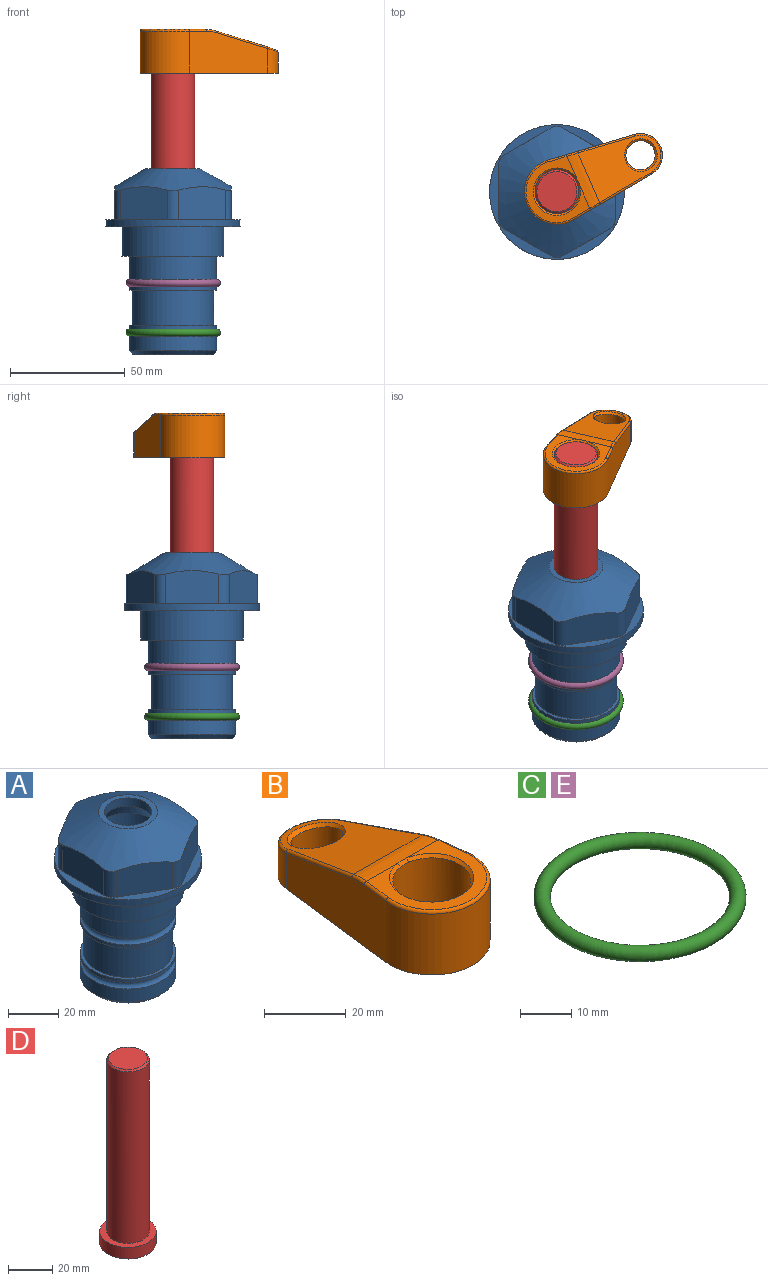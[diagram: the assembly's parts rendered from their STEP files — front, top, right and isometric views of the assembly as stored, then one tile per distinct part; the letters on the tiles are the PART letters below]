
ASSEMBLY  parts=5 mates=4
PART A: 36 faces, bbox 58.7x58.7x81 mm
  f0: cylinder r=17.78mm len=35.56mm, axis (0,0,1), area 1670.8mm2, adj f23,f24,f31
  f1: cylinder r=19.05mm len=38.1mm, axis (0,0,1), area 1191.9mm2, adj f26,f27,f30
  f2: plane 58.66x58.66mm, normal (0,0,-1), area 1150.6mm2, adj f3,f28
  f3: cylinder r=29.33mm len=58.66mm, axis (0,0,-1), area 585.1mm2, adj f2,f4
  f4: plane 58.66x58.66mm, normal (0,0,1), area 475.9mm2, adj f3,f5,f6,f7,f8,f9,f10,f11
  f5: plane 20.32x14.34mm, normal (-0.5,0.87,0), area 324.4mm2, adj f4,f15,f16,f17
  f6: plane 20.32x14.34mm, normal (0.5,0.87,0), area 324.4mm2, adj f4,f14,f15,f17
  f7: plane 23.48x14.34mm, normal (1,0,0), area 324.4mm2, adj f4,f13,f14,f17
  f8: plane 20.32x14.34mm, normal (0.5,-0.87,0), area 324.4mm2, adj f4,f12,f13,f17
  f9: plane 20.32x14.34mm, normal (-0.5,-0.87,0), area 324.4mm2, adj f4,f11,f12,f17
  f10: plane 23.48x14.34mm, normal (-1,0,0), area 324.4mm2, adj f4,f11,f16,f17
  f11: cylinder r=5.08mm len=12.85mm, axis (0,0,-1), area 67.2mm2, adj f4,f9,f10,f17
  f12: cylinder r=5.08mm len=12.85mm, axis (0,0,-1), area 67.2mm2, adj f4,f8,f9,f17
  f13: cylinder r=5.08mm len=12.85mm, axis (0,0,-1), area 67.2mm2, adj f4,f7,f8,f17
  f14: cylinder r=5.08mm len=12.85mm, axis (0,0,-1), area 67.2mm2, adj f4,f6,f7,f17
  f15: cylinder r=5.08mm len=12.85mm, axis (0,0,-1), area 67.2mm2, adj f4,f5,f6,f17
  f16: cylinder r=5.08mm len=12.85mm, axis (0,0,-1), area 67.2mm2, adj f4,f5,f10,f17
  f17: cone r=11.73mm half-angle=60deg, axis (0,0,-1), area 2071.8mm2, adj f5,f6,f7,f8,f9,f10,f11,f12
  f18: plane 23.46x23.46mm, normal (0,0,1), area 147.4mm2, adj f17,f35
  f19: plane 34.93x34.93mm, normal (0,0,-1), area 958mm2, adj f29
  f20: cylinder r=19.05mm len=38.1mm, axis (0,0,1), area 760.1mm2, adj f21,f29
  f21: torus R=19.05mm, axis (0,0,1), area 565.3mm2, adj f20,f22
  f22: cylinder r=19.05mm len=38.1mm, axis (0,0,1), area 190mm2, adj f21,f23
  f23: plane 38.1x38.1mm, normal (0,0,1), area 146.9mm2, adj f0,f22
  f24: plane 38.1x38.1mm, normal (0,0,-1), area 146.9mm2, adj f0,f25
  f25: cylinder r=19.05mm len=38.1mm, axis (0,0,1), area 190mm2, adj f24,f26
  f26: torus R=19.05mm, axis (0,0,1), area 565.3mm2, adj f1,f25
  f27: plane 44.45x44.45mm, normal (0,0,-1), area 411.7mm2, adj f1,f28
  f28: cylinder r=22.23mm len=44.45mm, axis (0,0,1), area 1773.5mm2, adj f2,f27
  f29: cone r=19.05mm half-angle=45deg, axis (0,0,1), area 257.5mm2, adj f19,f20
  f30: cylinder r=3.17mm len=6.75mm, axis (-1,0,0), area 128mm2, adj f1,f33
  f31: cylinder r=3.17mm len=6.35mm, axis (-1,0,0), area 102.5mm2, adj f0,f33
  f32: plane 25.4x25.4mm, normal (0,0,1), area 506.7mm2, adj f33
  f33: cylinder r=12.7mm len=66.42mm, axis (0,0,-1), area 5236.2mm2, adj f30,f31,f32,f34
  f34: cone r=9.53mm half-angle=30deg, axis (0,0,-1), area 443.4mm2, adj f33,f35
  f35: cylinder r=9.53mm len=19.05mm, axis (0,0,-1), area 240.9mm2, adj f18,f34
PART B: 31 faces, bbox 31.7x65.5x19.8 mm
  f0: plane 39.12x18.26mm, normal (0.99,0.12,0), area 612.2mm2, adj f1,f4,f7,f11,f13,f15
  f1: cylinder r=9.53mm len=18.91mm, axis (0,0,-1), area 296.1mm2, adj f0,f2,f7,f17
  f2: plane 39.12x18.26mm, normal (-0.99,0.12,0), area 612.2mm2, adj f1,f4,f7,f12,f14,f16
  f3: cylinder r=6.35mm len=12.7mm, axis (0,0,-1), area 362.4mm2, adj f7,f18
  f4: cylinder r=14.29mm len=28.58mm, axis (0,0,-1), area 882.2mm2, adj f0,f2,f7,f10
  f5: cylinder r=9.53mm len=19.05mm, axis (0,0,-1), area 1092.6mm2, adj f7,f19,f20
  f6: plane 26.99x23.69mm, normal (0,0,1), area 216.2mm2, adj f9,f10,f11,f12,f19
  f7: plane 63.5x28.58mm, normal (0,0,-1), area 661.8mm2, adj f0,f1,f2,f3,f4,f5,f22,f23
  f8: plane 33.52x23.6mm, normal (0,0.26,0.97), area 486mm2, adj f9,f15,f16,f17,f18
  f9: cylinder r=19.05mm len=24.72mm, axis (1,0,0), area 120.4mm2, adj f6,f8,f13,f14,f20
  f10: torus R=13.49mm, axis (0,0,1), area 59mm2, adj f4,f6,f11,f12
  f11: cylinder r=0.79mm len=8.67mm, axis (0.12,-0.99,0), area 10.8mm2, adj f0,f6,f10,f13
  f12: cylinder r=0.79mm len=8.67mm, axis (0.12,0.99,0), area 10.8mm2, adj f2,f6,f10,f14
  f13: bspline ~4.95x1.42mm, area 6.1mm2, adj f0,f9,f11,f15
  f14: bspline ~4.95x1.42mm, area 6.1mm2, adj f2,f9,f12,f16
  f15: cylinder r=0.79mm len=25.95mm, axis (0.12,-0.96,0.26), area 32.9mm2, adj f0,f8,f13,f17
  f16: cylinder r=0.79mm len=25.95mm, axis (0.12,0.96,-0.26), area 32.9mm2, adj f2,f8,f14,f17
  f17: bspline ~18.91x8.38mm, area 30mm2, adj f1,f8,f15,f16
  f18: bspline ~14.29x14.29mm, area 48.3mm2, adj f3,f8
  f19: cone r=9.53mm half-angle=45deg, axis (0,0,1), area 66.5mm2, adj f5,f6,f20
  f20: bspline ~3.22x0.96mm, area 3.5mm2, adj f5,f9,f19
  f21: plane 2.75x2.72mm, normal (0,0,-1), area 2.9mm2, adj f23,f25,f28
  f22: plane 23.05x15.88mm, normal (-0.99,-0.12,0), area 323.6mm2, adj f7,f25,f26,f27,f28,f29
  f23: plane 23.05x15.88mm, normal (0.99,-0.12,0), area 323.6mm2, adj f7,f21,f25,f27,f28,f30
  f24: cylinder r=9.53mm len=10.69mm, axis (0,0,-1), area 114.7mm2, adj f7,f27,f29,f30
  f25: cylinder r=12.7mm len=20.59mm, axis (0,0,-1), area 381.1mm2, adj f7,f21,f22,f23,f26,f28
  f26: plane 2.75x2.72mm, normal (0,0,-1), area 2.9mm2, adj f22,f25,f28
  f27: plane 19.72x18.37mm, normal (0,-0.26,-0.97), area 291.8mm2, adj f22,f23,f24,f28,f29,f30
  f28: cylinder r=15.88mm len=19.92mm, axis (1,0,0), area 54.8mm2, adj f21,f22,f23,f25,f26,f27
  f29: cylinder r=1.59mm len=11mm, axis (0,0,-1), area 34.7mm2, adj f7,f22,f24,f27
  f30: cylinder r=1.59mm len=11mm, axis (0,0,-1), area 34.7mm2, adj f7,f23,f24,f27
PART C: 1 faces, bbox 44.7x44.7x3.2 mm
  f0: torus R=19.05mm, axis (0,0,1), area 1193.9mm2
PART D: 6 faces, bbox 25.4x25.4x101.6 mm
  f0: plane 17.46x17.46mm, normal (0,0,1), area 239.5mm2, adj f5
  f1: plane 25.4x25.4mm, normal (0,0,-1), area 506.7mm2, adj f2
  f2: cylinder r=12.7mm len=25.4mm, axis (0,0,1), area 506.7mm2, adj f1,f3
  f3: plane 25.4x25.4mm, normal (0,0,1), area 221.7mm2, adj f2,f4
  f4: cylinder r=9.53mm len=94.46mm, axis (0,0,1), area 5653mm2, adj f3,f5
  f5: cone r=8.73mm half-angle=45deg, axis (0,0,-1), area 64.4mm2, adj f0,f4
PART E: same geometry as C
PLACE A t=(234.9,63.93,301.05)mm fixed
PLACE B rot(axis=(0,0,-1),66.5deg) t=(234.9,63.93,323.52)mm
PLACE C t=(234.9,63.93,279.46)mm
PLACE D rot(axis=(0,0,-1),66.5deg) t=(234.9,63.93,323.52)mm
PLACE E t=(234.9,63.93,301.05)mm
MATE fastened B.f4 <-> D.f2  axis (0,0,1) through (234.9,63.93,387.02)mm
MATE fastened E.f0 <-> A.f0  axis (0,0,1) through (234.9,63.93,276.54)mm
MATE cylindrical A.f0 <-> D.f2  axis (0,0,1) through (234.9,63.93,250.5)mm
MATE fastened C.f0 <-> A.f0  axis (0,0,1) through (234.9,63.93,254.95)mm
